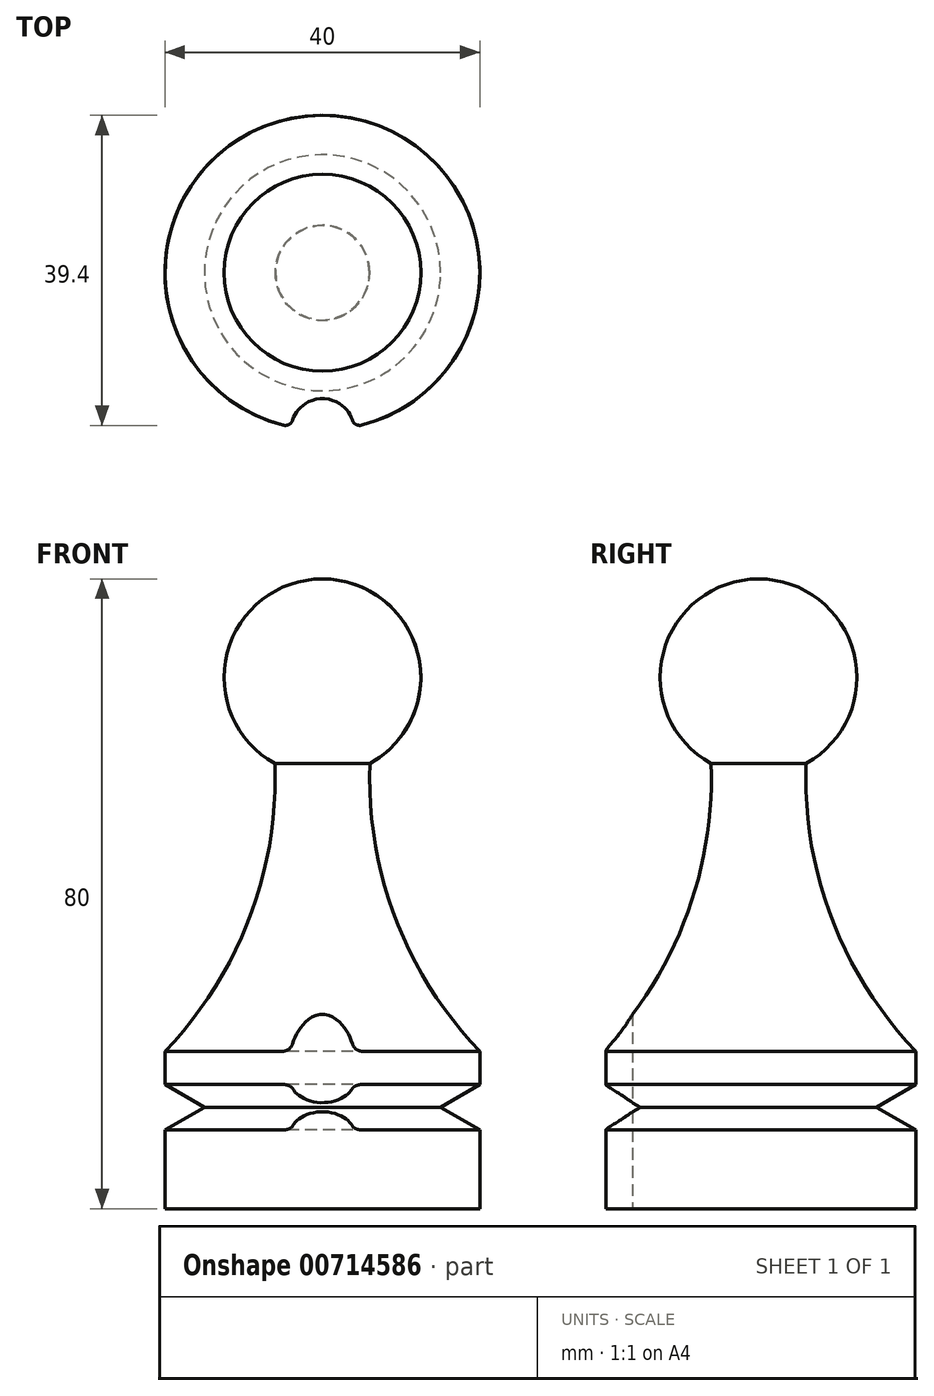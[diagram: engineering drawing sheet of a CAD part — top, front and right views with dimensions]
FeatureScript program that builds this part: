
annotation { "Feature Type Name" : "Feature", "Feature Type Description" : "" }
export const myFeature = defineFeature(function(context is Context, id is Id, definition is map)
    precondition{}
    {
        {
            var Q0;
            Q0=qCreatedBy(makeId("Front.planeOp"),FACE);
            var sketch = newSketch(context, id + "F0", { "sketchPlane" : qUnion([Q0])});
            skLineSegment(sketch, "E0", {"start": v(0, 80) * mm, "end": v(0, -97.06) * mm, "construction": true});
            skLineSegment(sketch, "E1", {"start": v(0, 0) * mm, "end": v(20, 0) * mm});
            skLineSegment(sketch, "E2", {"start": v(20, 0) * mm, "end": v(20, 10) * mm});
            skLineSegment(sketch, "E3", {"start": v(15, 12.89) * mm, "end": v(20, 10) * mm});
            skLineSegment(sketch, "E4", {"start": v(15, 12.89) * mm, "end": v(20, 15.77) * mm});
            skLineSegment(sketch, "E5", {"start": v(20, 15.77) * mm, "end": v(20, 20) * mm});
            skArc(sketch, "E6", {"start": v(6.03, 56.55) * mm, "mid": v(9.3, 36.85) * mm, "end": v(20, 20) * mm});
            skArc(sketch, "E7", {"start": v(6.03, 56.55) * mm, "mid": v(12.1, 70.62) * mm, "end": v(0, 80) * mm});
            skLineSegment(sketch, "E8", {"start": v(0, 80) * mm, "end": v(0, -28.62) * mm});
            skSolve(sketch);
        }
        {
            var Q0;
            {var subQ0=sQuery(id+"F0.wireOp",EDGE,"E1");Q0=makeQuery(id+"F0.imprint","IMPRINT",FACE,{"disambiguationData":[TD([[makeQuery(id+"F0.imprint","IMPRINT",EDGE,{"derivedFrom":subQ0}),1.0]])]});}
            var Q1;
            Q1=sQuery(id+"F0.wireOp",EDGE,"E8");
            revolve(context, id + "F1", {"surfaceOperationType" : NewSurfaceOperationType.NEW, "entities" : qUnion([Q0]), "axis" : qUnion([Q1]), "revolveType" : RevolveType.FULL});
        }
        {
            var Q0;
            Q0=makeQuery(id+"F1.opRevolve","SWEPT_FACE",FACE,{"disambiguationData":[OSD([sQuery(id+"F0.wireOp",EDGE,"E1")])]});
            var sketch = newSketch(context, id + "F2", { "sketchPlane" : qUnion([Q0])});
            skCircle(sketch, "E9", {"center": v(0, 20) * mm, "radius": 4 * mm});
            skSolve(sketch);
        }
        {
            var Q0;
            Q0 = qSketchRegion(id + "F2", true);
            extrude(context, id + "F3", {"entities" : qUnion([Q0]), "operationType" : NewBodyOperationType.REMOVE, "oppositeDirection" : true, "depth" : 25 * mm, "offsetDistance" : 25 * mm});
        }
        {
            var Q0;
            Q0=makeQuery(id+"F3.boolean.opBoolean","INTERSECT",EDGE,{"disambiguationData":[OD(0.0)],"derivedFrom":[makeQuery(id+"F1.opRevolve","SWEPT_FACE",FACE,{"disambiguationData":[OSD([sQuery(id+"F0.wireOp",EDGE,"E5")])]}),makeQuery(id+"F3.opExtrude","SWEPT_FACE",FACE,{"disambiguationData":[OSD([sQuery(id+"F2.wireOp",EDGE,"E9")])]})]});
            var Q1;
            Q1=makeQuery(id+"F3.boolean.opBoolean","INTERSECT",EDGE,{"disambiguationData":[OD(1.0)],"derivedFrom":[makeQuery(id+"F1.opRevolve","SWEPT_FACE",FACE,{"disambiguationData":[OSD([sQuery(id+"F0.wireOp",EDGE,"E5")])]}),makeQuery(id+"F3.opExtrude","SWEPT_FACE",FACE,{"disambiguationData":[OSD([sQuery(id+"F2.wireOp",EDGE,"E9")])]})]});
            var Q2;
            Q2=makeQuery(id+"F3.boolean.opBoolean","INTERSECT",EDGE,{"disambiguationData":[OD(0.0)],"derivedFrom":[makeQuery(id+"F1.opRevolve","SWEPT_FACE",FACE,{"disambiguationData":[OSD([sQuery(id+"F0.wireOp",EDGE,"E2")])]}),makeQuery(id+"F3.opExtrude","SWEPT_FACE",FACE,{"disambiguationData":[OSD([sQuery(id+"F2.wireOp",EDGE,"E9")])]})]});
            var Q3;
            Q3=makeQuery(id+"F3.boolean.opBoolean","INTERSECT",EDGE,{"disambiguationData":[OD(1.0)],"derivedFrom":[makeQuery(id+"F1.opRevolve","SWEPT_FACE",FACE,{"disambiguationData":[OSD([sQuery(id+"F0.wireOp",EDGE,"E2")])]}),makeQuery(id+"F3.opExtrude","SWEPT_FACE",FACE,{"disambiguationData":[OSD([sQuery(id+"F2.wireOp",EDGE,"E9")])]})]});
            fillet(context, id + "F4", {"entities" : qUnion([Q0, Q1, Q2, Q3]), "radius" : 1 * mm, "tangentPropagation" : true, "allowEdgeOverflow" : false});
        }
    });
